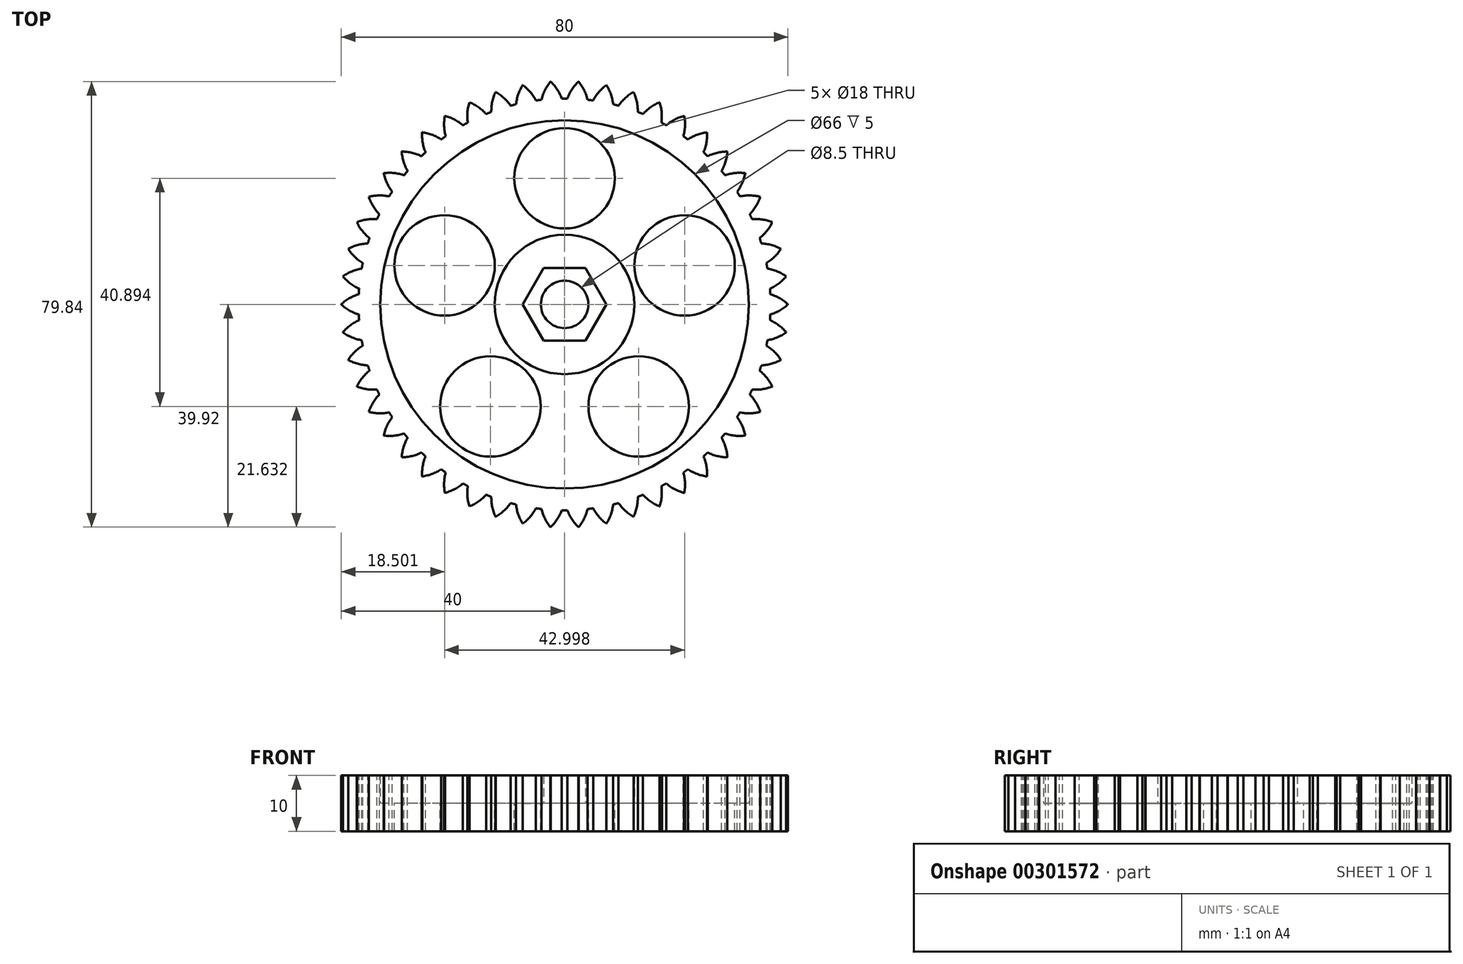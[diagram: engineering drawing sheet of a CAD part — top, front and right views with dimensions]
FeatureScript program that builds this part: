
annotation { "Feature Type Name" : "Feature", "Feature Type Description" : "" }
export const myFeature = defineFeature(function(context is Context, id is Id, definition is map)
    precondition{}
    {
        {
            var Q0;
            Q0=qCreatedBy(makeId("Top.planeOp"),FACE);
            var sketch = newSketch(context, id + "F0", { "sketchPlane" : qUnion([Q0])});
            skCircle(sketch, "E0", {"center": v(0, 0) * mm, "radius": 40 * mm});
            skSolve(sketch);
        }
        {
            var Q0;
            Q0=makeQuery(id+"F0.imprint","IMPRINT",FACE,{"disambiguationData":[TD([[makeQuery(id+"F0.imprint","IMPRINT",EDGE,{"derivedFrom":sQuery(id+"F0.wireOp",EDGE,"E0")}),1.0]])]});
            extrude(context, id + "F1", {"entities" : qUnion([Q0]), "depth" : 5 * mm});
        }
        {
            var Q0;
            Q0=makeQuery(id+"F1.opExtrude","CAP_FACE",FACE,{"disambiguationData":[OSD([sQuery(id+"F0.wireOp",EDGE,"E0")])],"isStart":false});
            var sketch = newSketch(context, id + "F2", { "sketchPlane" : qUnion([Q0])});
            skCircle(sketch, "E1", {"center": v(0, 0) * mm, "radius": 40 * mm});
            skCircle(sketch, "E2", {"center": v(0, 0) * mm, "radius": 33 * mm});
            skSolve(sketch);
        }
        {
            var Q0;
            Q0=makeQuery(id+"F2.imprint","IMPRINT",FACE,{"disambiguationData":[TD([[makeQuery(id+"F2.imprint","IMPRINT",EDGE,{"derivedFrom":sQuery(id+"F2.wireOp",EDGE,"E1")}),1.0]])]});
            extrude(context, id + "F3", {"entities" : qUnion([Q0]), "operationType" : NewBodyOperationType.ADD, "depth" : 5 * mm});
        }
        {
            var Q0;
            Q0=makeQuery(id+"F1.opExtrude","CAP_FACE",FACE,{"disambiguationData":[OSD([sQuery(id+"F0.wireOp",EDGE,"E0")])],"isStart":false});
            var sketch = newSketch(context, id + "F4", { "sketchPlane" : qUnion([Q0])});
            skCircle(sketch, "E3", {"center": v(0, 0) * mm, "radius": 4.25 * mm});
            skSolve(sketch);
        }
        {
            var Q0;
            Q0=makeQuery(id+"F4.imprint","IMPRINT",FACE,{"disambiguationData":[TD([[makeQuery(id+"F4.imprint","IMPRINT",EDGE,{"derivedFrom":sQuery(id+"F4.wireOp",EDGE,"E3")}),1.0]])]});
            extrude(context, id + "F5", {"entities" : qUnion([Q0]), "operationType" : NewBodyOperationType.REMOVE, "endBound" : BoundingType.UP_TO_NEXT, "oppositeDirection" : true, "depth" : 25 * mm});
        }
        {
            var Q0;
            Q0=makeQuery(id+"F1.opExtrude","CAP_FACE",FACE,{"disambiguationData":[OSD([sQuery(id+"F0.wireOp",EDGE,"E0")])],"isStart":false});
            var sketch = newSketch(context, id + "F6", { "sketchPlane" : qUnion([Q0])});
            skCircle(sketch, "E4", {"center": v(0, 0) * mm, "radius": 12.5 * mm});
            skCircle(sketch, "E5.cCircle", {"center": v(0, 0) * mm, "radius": 6.5 * mm, "construction": true});
            skLineSegment(sketch, "E5.0", {"start": v(-7.5, 0) * mm, "end": v(-3.75, 6.5) * mm});
            skLineSegment(sketch, "E5.1", {"start": v(-3.75, 6.5) * mm, "end": v(3.75, 6.5) * mm});
            skLineSegment(sketch, "E5.2", {"start": v(3.75, 6.5) * mm, "end": v(7.5, 0) * mm});
            skLineSegment(sketch, "E5.3", {"start": v(7.5, 0) * mm, "end": v(3.75, -6.5) * mm});
            skLineSegment(sketch, "E5.4", {"start": v(3.75, -6.5) * mm, "end": v(-3.75, -6.5) * mm});
            skLineSegment(sketch, "E5.5", {"start": v(-3.75, -6.5) * mm, "end": v(-7.5, 0) * mm});
            skPoint(sketch, "E5.0.midPoint", {"position": v(-5.63, 3.25) * mm});
            skSolve(sketch);
        }
        {
            var Q0;
            Q0=makeQuery(id+"F6.imprint","IMPRINT",FACE,{"disambiguationData":[TD([[makeQuery(id+"F6.imprint","IMPRINT",EDGE,{"derivedFrom":sQuery(id+"F6.wireOp",EDGE,"E4")}),1.0]])]});
            extrude(context, id + "F7", {"entities" : qUnion([Q0]), "operationType" : NewBodyOperationType.ADD, "depth" : 5 * mm});
        }
        {
            var Q0;
            Q0=makeQuery(id+"F7.boolean.opBoolean","SPLIT",FACE,{"disambiguationData":[TD([makeQuery(id+"F3.opExtrude","SWEPT_FACE",FACE,{"disambiguationData":[OSD([sQuery(id+"F2.wireOp",EDGE,"E2")])]})])],"derivedFrom":makeQuery(id+"F1.opExtrude","CAP_FACE",FACE,{"disambiguationData":[OSD([sQuery(id+"F0.wireOp",EDGE,"E0")])],"isStart":false})});
            var sketch = newSketch(context, id + "F8", { "sketchPlane" : qUnion([Q0])});
            skCircle(sketch, "E6", {"center": v(0, 22.6) * mm, "radius": 9 * mm});
            skCircle(sketch, "E7.1.0", {"center": v(-21.5, 6.99) * mm, "radius": 9 * mm});
            skCircle(sketch, "E7.2.0", {"center": v(-13.29, -18.29) * mm, "radius": 9 * mm});
            skCircle(sketch, "E7.3.0", {"center": v(13.29, -18.29) * mm, "radius": 9 * mm});
            skCircle(sketch, "E7.4.0", {"center": v(21.5, 6.99) * mm, "radius": 9 * mm});
            skPoint(sketch, "E7.center", {"position": v(0, 0) * mm});
            skSolve(sketch);
        }
        {
            var Q0;
            Q0=qSketchRegion(id+"F8",true);
            extrude(context, id + "F9", {"entities" : qUnion([Q0]), "operationType" : NewBodyOperationType.REMOVE, "endBound" : BoundingType.UP_TO_NEXT, "oppositeDirection" : true, "depth" : 25 * mm});
        }
        {
            var Q0;
            Q0=makeQuery(id+"F3.opExtrude","CAP_FACE",FACE,{"disambiguationData":[OSD([sQuery(id+"F2.wireOp",EDGE,"E1"),sQuery(id+"F2.wireOp",EDGE,"E2")])],"isStart":false});
            var sketch = newSketch(context, id + "F10", { "sketchPlane" : qUnion([Q0])});
            skArc(sketch, "E8", {"start": v(2.5, 39.92) * mm, "mid": v(0, 40) * mm, "end": v(-2.5, 39.92) * mm});
            skArc(sketch, "E9", {"start": v(0.5, 36.9) * mm, "mid": v(0, 36.9) * mm, "end": v(-0.5, 36.9) * mm});
            skArc(sketch, "E10", {"start": v(-0.5, 36.9) * mm, "mid": v(-1.33, 38.52) * mm, "end": v(-2.5, 39.92) * mm});
            skArc(sketch, "E11.MirrorCS", {"start": v(0.5, 36.9) * mm, "mid": v(1.33, 38.52) * mm, "end": v(2.5, 39.92) * mm});
            skSolve(sketch);
        }
        {
            var Q0;
            Q0=makeQuery(id+"F10.imprint","IMPRINT",FACE,{"disambiguationData":[TD([[makeQuery(id+"F10.imprint","IMPRINT",EDGE,{"derivedFrom":sQuery(id+"F10.wireOp",EDGE,"E8")}),1.0]])]});
            extrude(context, id + "F11", {"entities" : qUnion([Q0]), "operationType" : NewBodyOperationType.REMOVE, "endBound" : BoundingType.UP_TO_NEXT, "oppositeDirection" : true, "depth" : 25 * mm});
        }
        {
            var Q0;
            Q0=makeQuery(id+"F11.boolean.opBoolean","COPY",FACE,{"derivedFrom":makeQuery(id+"F11.opExtrude","SWEPT_FACE",FACE,{"disambiguationData":[OSD([sQuery(id+"F10.wireOp",EDGE,"E10")])]})});
            var Q1;
            Q1=makeQuery(id+"F11.boolean.opBoolean","COPY",FACE,{"derivedFrom":makeQuery(id+"F11.opExtrude","SWEPT_FACE",FACE,{"disambiguationData":[OSD([sQuery(id+"F10.wireOp",EDGE,"E11.MirrorCS")])]})});
            var Q2;
            Q2=makeQuery(id+"F11.boolean.opBoolean","COPY",FACE,{"derivedFrom":makeQuery(id+"F11.opExtrude","SWEPT_FACE",FACE,{"disambiguationData":[OSD([sQuery(id+"F10.wireOp",EDGE,"E9")])]})});
            var Q3;
            Q3=makeQuery(id+"F3.boolean.opBoolean","MERGE",FACE,{"derivedFrom":[makeQuery(id+"F1.opExtrude","SWEPT_FACE",FACE,{"disambiguationData":[OSD([sQuery(id+"F0.wireOp",EDGE,"E0")])]}),makeQuery(id+"F3.opExtrude","SWEPT_FACE",FACE,{"disambiguationData":[OSD([sQuery(id+"F2.wireOp",EDGE,"E1")])]})]});
            circularPattern(context, id + "F12", {"patternType" : PatternType.FACE, "faces" : qUnion([Q0, Q1, Q2]), "axis" : qUnion([Q3]), "angle" : 360 * degree, "instanceCount" : 50, "equalSpace" : true});
        }
    });
